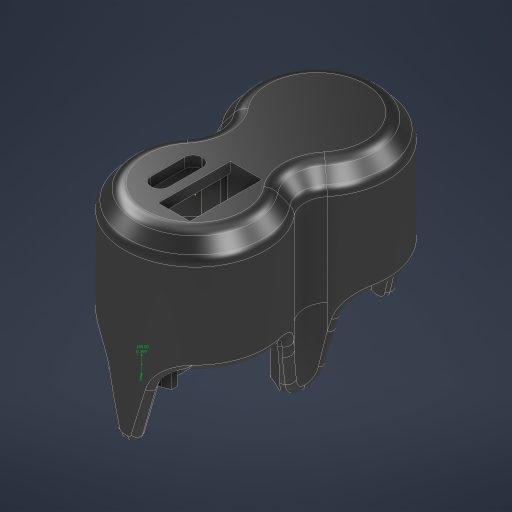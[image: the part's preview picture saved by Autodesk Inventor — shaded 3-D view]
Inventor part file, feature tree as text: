
AUTODESK INVENTOR PART (.ipt)
format: ipt  version: 2024 (Build 280153000, 153)  size: 1,166,848 bytes
history: native  units: mm
features: sketch x18, extrude x15, fillet x13, draft x4, chamfer x4, mirror x2, plane x2
ambient origin geometry x8: Origin, YZ Plane, XZ Plane, XY Plane, X Axis, Y Axis, Z Axis, Center Point
bodies: Solid1 (feature_tree)
feature tree (58):
  extrude  "Extrusion1"  Depth=23.0mm
  extrude  "Extrusion2"  Depth=27.0mm
  fillet  "Fillet1"  Radius=27.0mm
  extrude  "Extrusion3"  Depth=23.0mm
  fillet  "Fillet4"  [1 undecoded]
  extrude  "Extrusion4"  Depth=5.0mm
  extrude  "Extrusion5"  Depth=7.0mm
  extrude  "Extrusion9"  Depth=3.0mm TaperAngle=0.0deg
  mirror  "Mirror1"
  draft  "FaceDraft1"
  draft  "FaceDraft2"
  draft  "FaceDraft3"
  draft  "FaceDraft4"
  fillet  "Fillet8"  Radius=0.75mm
  fillet  "Fillet9"  Radius=23.0mm
  fillet  "Fillet10"  [1 undecoded]
  fillet  "Fillet11"  Radius=21.0mm
  fillet  "Fillet12"  Radius=21.0mm
  chamfer  "Chamfer1"  Distance=3.0mm
  extrude  "Extrusion14"  Depth=3.0mm
  chamfer  "Chamfer2"  Distance=3.0mm
  chamfer  "Chamfer3"  Distance=14.0mm
  fillet  "Fillet13"  [1 undecoded]
  fillet  "Fillet14"  [1 undecoded]
  fillet  "Fillet15"  [1 undecoded]
  sketch  "Sketch15"  dims[d61=4.25mm d62=1.25mm]
  plane  "Work Plane1"
  plane  "Work Plane2"
  mirror  "Mirror2"
  fillet  "Fillet16"  [1 undecoded]
  fillet  "Fillet17"  Radius=4.25mm
  extrude  "Extrusion15"  Depth=1.25mm
  extrude  "Extrusion16"  Depth=1.25mm
  fillet  "Fillet18"  Radius=5.75mm
  extrude  "Extrusion17"  Depth=1.0mm
  extrude  "Extrusion18"  Depth=2.5mm
  extrude  "Extrusion19"  TaperAngle=0.0deg  [1 undecoded]
  extrude  "Extrusion20"  Depth=8.0mm TaperAngle=0.0deg
  sketch  "Sketch24"  dims[d113=-23.3mm d114=-11.65mm d115=2.5mm]
  extrude  "Extrusion26"  Depth=3.0mm
  sketch  "Sketch30"  dims[d118=0.0mm d119=8.0mm d120=0.0mm]
  extrude  "Extrusion27"  Depth=3.0mm
  chamfer  "Chamfer5"  Distance=10.0mm
  sketch  "Sketch1"  dims[d0=23.0mm d1=23.0mm]
  sketch  "Sketch2"  dims[d2=0.3mm d3=27.0mm d4=27.0mm]
  sketch  "Sketch3"  dims[d5=22.0mm d6=0.0mm d7=23.0mm d8=0.0mm]
  sketch  "Sketch4"  dims[d9=2.0mm d10=0.0mm d11=5.0mm]
  sketch  "Sketch5"  dims[d14=23.0mm d15=7.0mm]
  sketch  "Sketch9"  dims[d16=7.0mm d17=20.0mm d18=0.0mm d19=0.75mm d20=23.0mm d21=0.0mm d22=21.0mm d23=21.0mm d24=3.0mm d25=0.0mm]
  sketch  "Sketch14"  dims[d26=1.0mm d27=1.0mm d28=3.0mm d29=0.0mm d54=14.0mm d55=0.0mm d56=15.0deg d57=15.0deg d58=15.0deg d59=15.0deg d60=4.25mm]
  sketch  "Sketch16"  dims[d63=1.25mm d64=1.25mm]
  sketch  "Sketch17"  dims[d95=3.0mm d96=2.0mm d97=8.726646mm]
  sketch  "Sketch18"  dims[d100=14.0mm d101=7.0mm d102=0.0mm d103=0.0mm]
  sketch  "Sketch19"  dims[d104=15.0mm d105=2.0mm d106=2.443461mm]
  sketch  "Sketch20"  dims[d107=15.0mm d108=2.0mm d109=2.443461mm d110=5.75mm]
  sketch  "Sketch21"  dims[d111=1.5mm d112=1.0mm]
  sketch  "Sketch29"  dims[d116=2.5mm d117=0.0mm]
  sketch  "Sketch31"  dims[d121=9.0mm d122=0.0mm d123=2.0mm d124=1.0mm d125=10.0mm d126=0.0mm d127=13.86mm d128=5.0mm d129=3.0mm d130=5.0mm d131=3.0mm d132=1.16mm d133=4.0mm d134=0.0mm d135=2.0mm d136=2.0mm d137=1.35mm d138=1.35mm d139=9.0mm d140=0.0mm d141=2.0mm d142=2.0mm d143=12.25mm d144=0.0mm d153=0.395mm d154=4.0mm d155=0.0mm d156=180.0deg d169=1.67mm d170=12.0mm d171=0.0mm d175=0.66mm d176=0.66mm d177=0.66mm d178=0.66mm d179=0.66mm d180=0.66mm d181=3.0mm d182=0.0mm d183=2.0mm d184=2.0mm d185=45.0deg d13=0.0mm d30=0.0mm d31=0.0mm d32=0.0mm d33=0.0mm]
note: 7 required parameter values undecoded (feature->parameter linkage not recoverable at this tier; creation-order binding heuristic only, values carry confidence <= 0.55)
